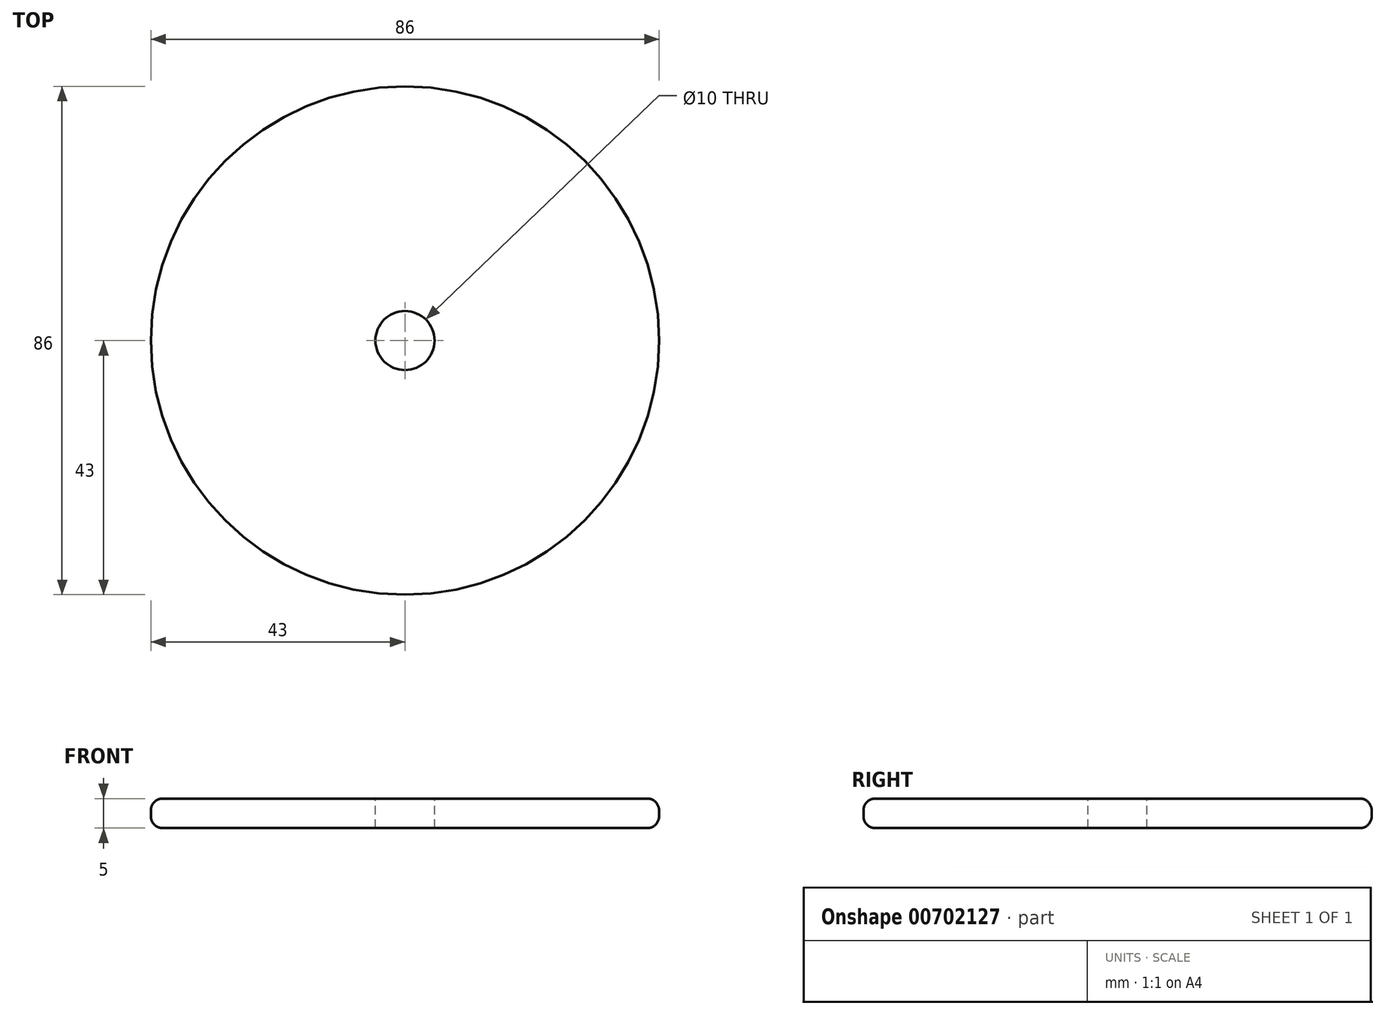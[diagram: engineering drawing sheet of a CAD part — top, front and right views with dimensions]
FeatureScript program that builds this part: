
annotation { "Feature Type Name" : "Feature", "Feature Type Description" : "" }
export const myFeature = defineFeature(function(context is Context, id is Id, definition is map)
    precondition{}
    {
        {
            var Q0;
            Q0=qCreatedBy(makeId("Top.planeOp"),FACE);
            var sketch = newSketch(context, id + "F0", { "sketchPlane" : qUnion([Q0])});
            skCircle(sketch, "E0", {"center": v(0, 0) * mm, "radius": 43 * mm});
            skSolve(sketch);
        }
        {
            var Q0;
            Q0=makeQuery(id+"F0.imprint","IMPRINT",FACE,{"disambiguationData":[TD([[makeQuery(id+"F0.imprint","IMPRINT",EDGE,{"derivedFrom":sQuery(id+"F0.wireOp",EDGE,"E0")}),1.0]])]});
            extrude(context, id + "F1", {"entities" : qUnion([Q0]), "depth" : 5 * mm, "offsetDistance" : 25 * mm});
        }
        {
            var Q0;
            Q0=makeQuery(id+"F1.opExtrude","CAP_FACE",FACE,{"disambiguationData":[OSD([sQuery(id+"F0.wireOp",EDGE,"E0")])],"isStart":false});
            var sketch = newSketch(context, id + "F2", { "sketchPlane" : qUnion([Q0])});
            skCircle(sketch, "E1", {"center": v(0, 0) * mm, "radius": 5 * mm});
            skSolve(sketch);
        }
        {
            var Q0;
            Q0=makeQuery(id+"F2.imprint","IMPRINT",FACE,{"disambiguationData":[TD([[makeQuery(id+"F2.imprint","IMPRINT",EDGE,{"derivedFrom":sQuery(id+"F2.wireOp",EDGE,"E1")}),1.0]])]});
            extrude(context, id + "F3", {"entities" : qUnion([Q0]), "operationType" : NewBodyOperationType.REMOVE, "endBound" : BoundingType.THROUGH_ALL, "oppositeDirection" : true, "depth" : 25 * mm, "offsetDistance" : 25 * mm});
        }
        {
            var Q0;
            Q0=makeQuery(id+"F1.opExtrude","CAP_EDGE",EDGE,{"disambiguationData":[OSD([sQuery(id+"F0.wireOp",EDGE,"E0")])],"isStart":true});
            var Q1;
            Q1=makeQuery(id+"F1.opExtrude","CAP_EDGE",EDGE,{"disambiguationData":[OSD([sQuery(id+"F0.wireOp",EDGE,"E0")])],"isStart":false});
            fillet(context, id + "F4", {"entities" : qUnion([Q0, Q1]), "radius" : 2 * mm, "tangentPropagation" : true, "allowEdgeOverflow" : false});
        }
    });
